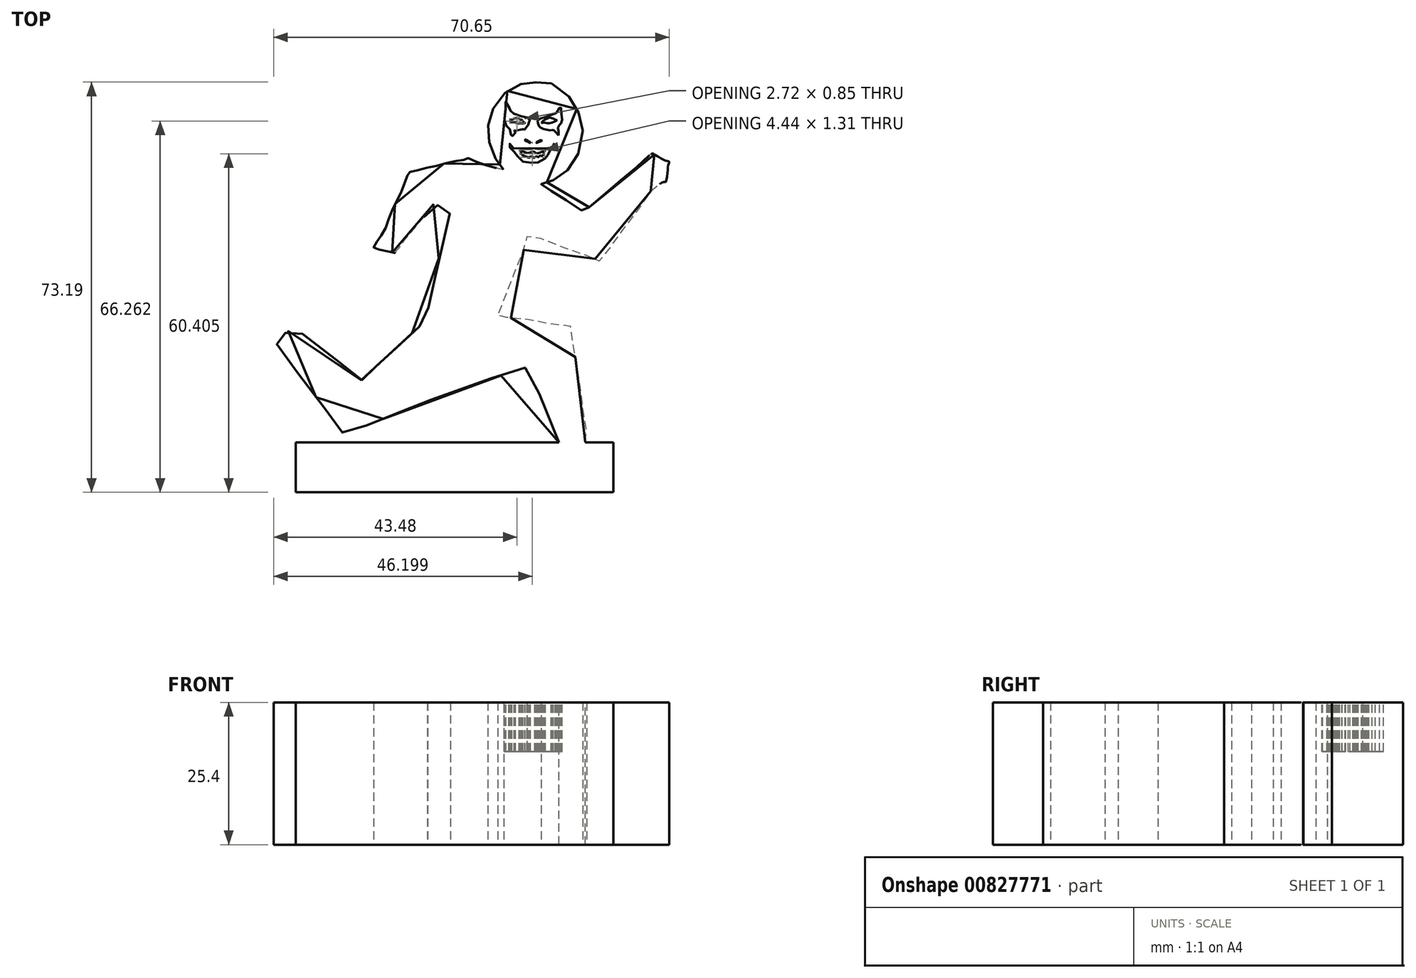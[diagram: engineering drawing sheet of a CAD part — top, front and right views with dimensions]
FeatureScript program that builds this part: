
annotation { "Feature Type Name" : "Feature", "Feature Type Description" : "" }
export const myFeature = defineFeature(function(context is Context, id is Id, definition is map)
    precondition{}
    {
        {
            var Q0;
            Q0=qCreatedBy(makeId("Top.planeOp"),FACE);
            var sketch = newSketch(context, id + "F0", { "sketchPlane" : qUnion([Q0])});
            skFitSpline(sketch, "E0", {"points": [v(-18.57, 4.15) * mm, v(-18.19, 6.36) * mm, v(-17.9, 8.2) * mm, v(-17.86, 8.65) * mm, v(-18.13, 9.75) * mm, v(-18.45, 11.85) * mm, v(-18.86, 15.21) * mm, v(-19.32, 18.61) * mm, v(-20.02, 22.59) * mm, v(-20.53, 26.32) * mm, v(-20.61, 27.35) * mm, v(-21.3, 27.55) * mm, v(-24.68, 27.94) * mm, v(-27.86, 28.57) * mm, v(-31.24, 28.92) * mm, v(-33.01, 29.13) * mm, v(-33.54, 29.19) * mm, v(-33.74, 29.28) * mm, v(-33.32, 30.3) * mm, v(-32.15, 33.5) * mm, v(-30.8, 36.86) * mm, v(-29.46, 40.17) * mm, v(-28.8, 42.23) * mm, v(-28.38, 43.77) * mm, v(-28.1, 44) * mm, v(-25.31, 42.81) * mm, v(-21.7, 41.41) * mm, v(-18.29, 40.28) * mm, v(-16.26, 39.46) * mm, v(-15.7, 39.1) * mm, v(-15.31, 39.32) * mm, v(-13.92, 41.12) * mm, v(-12.37, 43.38) * mm, v(-9, 47.86) * mm, v(-6.92, 50.75) * mm, v(-6.19, 51.93) * mm, v(-5.77, 52.26) * mm, v(-5.17, 52.66) * mm, v(-3.98, 53.25) * mm, v(-3.78, 53.22) * mm, v(-3.46, 54.96) * mm, v(-3.26, 56.4) * mm, v(-3.15, 56.8) * mm, v(-3.63, 56.97) * mm, v(-4.66, 57.47) * mm, v(-5.8, 58.12) * mm, v(-6.13, 58.31) * mm, v(-7.33, 57.4) * mm, v(-8.86, 55.97) * mm, v(-11.18, 54.03) * mm, v(-13.45, 52.12) * mm, v(-15.8, 50.1) * mm, v(-17.86, 48.26) * mm, v(-18.18, 47.89) * mm, v(-18.46, 47.96) * mm, v(-19.96, 48.87) * mm, v(-22.15, 50.4) * mm, v(-23.95, 51.46) * mm, v(-25.32, 52.34) * mm, v(-25.89, 52.72) * mm, v(-26.03, 52.96) * mm, v(-24.8, 53.2) * mm, v(-22.93, 54.05) * mm, v(-21.15, 55.45) * mm, v(-19.69, 57.6) * mm, v(-18.57, 61.62) * mm, v(-18.94, 64.38) * mm, v(-19.76, 66.54) * mm, v(-21.27, 68.72) * mm, v(-24.1, 70.74) * mm, v(-25.79, 70.95) * mm, v(-27.57, 71.03) * mm, v(-29.04, 70.86) * mm, v(-31.2, 69.95) * mm, v(-33.06, 68.54) * mm, v(-34.62, 66.1) * mm, v(-35.35, 63.99) * mm, v(-35.5, 62.12) * mm, v(-35.21, 60) * mm, v(-34.46, 57.88) * mm, v(-33.2, 56.14) * mm, v(-32.7, 55.5) * mm, v(-33.8, 55.63) * mm, v(-36.24, 56.34) * mm, v(-38.3, 57.1) * mm, v(-39.38, 57.5) * mm, v(-39.79, 57.18) * mm, v(-40.83, 57) * mm, v(-43.05, 56.57) * mm, v(-45.2, 55.97) * mm, v(-47.08, 55.56) * mm, v(-48.97, 55.06) * mm, v(-49.7, 54.93) * mm, v(-49.85, 54.55) * mm, v(-50.25, 53.43) * mm, v(-51.04, 51.35) * mm, v(-52.04, 49.37) * mm, v(-52.93, 47.45) * mm, v(-53.51, 45.7) * mm, v(-54.33, 43.98) * mm, v(-55.15, 42.91) * mm, v(-55.63, 41.9) * mm, v(-55.92, 41.43) * mm, v(-54.9, 41.14) * mm, v(-52.72, 40.62) * mm, v(-52.08, 40.47) * mm, v(-51.93, 40.79) * mm, v(-51.3, 41.51) * mm, v(-50.52, 42.7) * mm, v(-48.89, 44.6) * mm, v(-47.55, 46.27) * mm, v(-46.29, 47.66) * mm, v(-45.47, 48.87) * mm, v(-45.26, 49.22) * mm, v(-44.65, 49.12) * mm, v(-43.31, 48.79) * mm, v(-42.65, 48.66) * mm, v(-42.26, 48.5) * mm, v(-42.33, 47.66) * mm, v(-42.76, 46.23) * mm, v(-43.3, 43.25) * mm, v(-43.93, 40.96) * mm, v(-44.64, 37.9) * mm, v(-45.18, 34.92) * mm, v(-45.7, 32.63) * mm, v(-46.33, 29.56) * mm, v(-46.32, 28.72) * mm, v(-46.61, 28.55) * mm, v(-47.86, 27.33) * mm, v(-50.02, 25.33) * mm, v(-51.73, 23.7) * mm, v(-53.4, 22.14) * mm, v(-54.77, 20.94) * mm, v(-55.8, 20) * mm, v(-56.88, 18.93) * mm, v(-57.76, 18.1) * mm, v(-57.87, 17.9) * mm, v(-58.09, 17.85) * mm, v(-59.2, 18.82) * mm, v(-62.6, 21.46) * mm, v(-66.37, 24.44) * mm, v(-69.48, 26.81) * mm, v(-70.18, 27.28) * mm, v(-70.64, 26.95) * mm, v(-71.48, 26.4) * mm, v(-73.02, 25.57) * mm, v(-73.68, 25.26) * mm, v(-73.79, 25.07) * mm, v(-73.23, 24.27) * mm, v(-71.8, 22.23) * mm, v(-69.4, 19.03) * mm, v(-65.94, 14.44) * mm, v(-63.46, 11.27) * mm, v(-61.85, 9.03) * mm, v(-61.54, 8.55) * mm, v(-61.24, 8.13) * mm, v(-60.28, 8.47) * mm, v(-57.12, 9.8) * mm, v(-53.29, 11.31) * mm, v(-50.62, 12.42) * mm, v(-48.3, 13.44) * mm, v(-45.41, 14.45) * mm, v(-35.33, 18.05) * mm, v(-30.91, 19.34) * mm, v(-28.87, 20.1) * mm, v(-28.19, 20.07) * mm, v(-27.62, 18.72) * mm, v(-24.93, 11.88) * mm, v(-22.71, 6.44) * mm, v(-22.05, 4.72) * mm, v(-21.8, 4.28) * mm, v(-20.08, 4.35) * mm, v(-18.57, 4.15) * mm]});
            skSolve(sketch);
        }
        {
            var Q0;
            Q0 = qSketchRegion(id + "F0", true);
            extrude(context, id + "F1", {"entities" : qUnion([Q0]), "oppositeDirection" : true, "depth" : 25.4 * mm, "offsetDistance" : 25.4 * mm});
        }
        {
            var Q0;
            Q0=makeQuery(id+"F1.opExtrude","CAP_FACE",FACE,{"disambiguationData":[OSD([sQuery(id+"F0.wireOp",EDGE,"E0")])],"isStart":true});
            var sketch = newSketch(context, id + "F2", { "sketchPlane" : qUnion([Q0])});
            skFitSpline(sketch, "E1", {"points": [v(-31.67, 64.14) * mm, v(-31.52, 64.08) * mm, v(-31.41, 64.03) * mm, v(-31.33, 63.94) * mm, v(-31.24, 63.92) * mm, v(-31.1, 63.93) * mm, v(-31.04, 63.88) * mm, v(-30.93, 63.84) * mm, v(-30.77, 63.8) * mm, v(-30.64, 63.76) * mm, v(-30.5, 63.71) * mm, v(-30.36, 63.67) * mm, v(-30.2, 63.66) * mm, v(-30.09, 63.65) * mm, v(-30, 63.65) * mm, v(-29.9, 63.68) * mm, v(-29.8, 63.7) * mm, v(-29.67, 63.67) * mm, v(-29.5, 63.64) * mm, v(-29.37, 63.66) * mm, v(-29.2, 63.71) * mm, v(-29, 63.7) * mm, v(-28.89, 63.7) * mm, v(-28.9, 63.76) * mm, v(-28.97, 63.87) * mm, v(-29.08, 63.95) * mm, v(-29.22, 64.01) * mm, v(-29.35, 64.12) * mm, v(-29.5, 64.3) * mm, v(-29.6, 64.4) * mm, v(-29.73, 64.45) * mm, v(-30, 64.5) * mm, v(-30.23, 64.54) * mm, v(-30.4, 64.57) * mm, v(-30.58, 64.58) * mm, v(-30.74, 64.57) * mm, v(-30.97, 64.5) * mm, v(-31.18, 64.4) * mm, v(-31.38, 64.3) * mm, v(-31.53, 64.22) * mm, v(-31.67, 64.14) * mm]});
            skFitSpline(sketch, "E2", {"points": [v(-25.97, 63.88) * mm, v(-25.8, 64) * mm, v(-25.53, 64.2) * mm, v(-25.34, 64.35) * mm, v(-25.08, 64.5) * mm, v(-24.68, 64.65) * mm, v(-24.33, 64.66) * mm, v(-23.87, 64.5) * mm, v(-23.5, 64.35) * mm, v(-23.22, 64.22) * mm, v(-23.2, 64.21) * mm, v(-23.29, 64.15) * mm, v(-23.5, 64.05) * mm, v(-23.93, 63.88) * mm, v(-24.2, 63.78) * mm, v(-24.54, 63.7) * mm, v(-24.84, 63.7) * mm, v(-25.23, 63.77) * mm, v(-25.5, 63.81) * mm, v(-25.68, 63.83) * mm, v(-25.72, 63.83) * mm, v(-25.78, 63.76) * mm, v(-25.83, 63.76) * mm, v(-25.87, 63.76) * mm, v(-25.92, 63.8) * mm, v(-25.97, 63.88) * mm]});
            skFitSpline(sketch, "E3", {"points": [v(-26.82, 60.3) * mm, v(-26.6, 60.45) * mm, v(-26.33, 60.6) * mm, v(-26.15, 60.67) * mm, v(-26, 60.69) * mm, v(-25.91, 60.64) * mm, v(-25.9, 60.55) * mm, v(-25.95, 60.52) * mm, v(-26.08, 60.47) * mm, v(-26.23, 60.42) * mm, v(-26.34, 60.38) * mm, v(-26.4, 60.34) * mm, v(-26.52, 60.3) * mm, v(-26.66, 60.25) * mm, v(-26.79, 60.2) * mm, v(-26.9, 60.17) * mm, v(-26.9, 60.2) * mm, v(-26.82, 60.3) * mm]});
            skFitSpline(sketch, "E4", {"points": [v(-27.9, 60.19) * mm, v(-27.9, 60.23) * mm, v(-27.9, 60.24) * mm, v(-27.91, 60.26) * mm, v(-28.02, 60.36) * mm, v(-28.13, 60.43) * mm, v(-28.27, 60.5) * mm, v(-28.35, 60.55) * mm, v(-28.44, 60.6) * mm, v(-28.54, 60.69) * mm, v(-28.65, 60.75) * mm, v(-28.75, 60.78) * mm, v(-28.85, 60.77) * mm, v(-28.9, 60.73) * mm, v(-28.92, 60.7) * mm, v(-28.9, 60.63) * mm, v(-28.84, 60.55) * mm, v(-28.78, 60.51) * mm, v(-28.71, 60.5) * mm, v(-28.63, 60.5) * mm, v(-28.5, 60.44) * mm, v(-28.4, 60.38) * mm, v(-28.3, 60.34) * mm, v(-27.9, 60.19) * mm]});
            skFitSpline(sketch, "E5", {"points": [v(-25.3, 57.41) * mm, v(-25.26, 57.5) * mm, v(-25.2, 57.6) * mm, v(-25.08, 57.74) * mm, v(-24.94, 57.89) * mm, v(-24.8, 58.03) * mm, v(-24.73, 58.1) * mm, v(-24.66, 58.22) * mm, v(-24.6, 58.38) * mm, v(-24.49, 58.64) * mm, v(-24.43, 58.82) * mm, v(-24.41, 58.86) * mm, v(-24.36, 58.9) * mm, v(-24.3, 58.94) * mm, v(-24.23, 58.96) * mm, v(-24.25, 59.03) * mm, v(-24.22, 59.09) * mm, v(-24.15, 59.06) * mm, v(-24.13, 59.12) * mm, v(-24.04, 59.15) * mm, v(-23.94, 59.18) * mm, v(-23.87, 59.21) * mm, v(-23.83, 59.3) * mm, v(-23.84, 59.35) * mm, v(-23.86, 59.4) * mm, v(-23.85, 59.44) * mm, v(-23.85, 59.48) * mm, v(-23.83, 59.5) * mm, v(-23.78, 59.47) * mm, v(-23.69, 59.43) * mm, v(-23.62, 59.44) * mm, v(-23.53, 59.5) * mm, v(-23.45, 59.56) * mm, v(-23.37, 59.69) * mm, v(-23.33, 59.8) * mm, v(-23.37, 59.91) * mm, v(-23.44, 60) * mm, v(-23.54, 60.06) * mm, v(-23.62, 60.1) * mm, v(-23.69, 60.09) * mm, v(-23.73, 60.05) * mm, v(-23.79, 59.99) * mm, v(-23.84, 59.94) * mm, v(-23.88, 59.87) * mm, v(-23.88, 59.83) * mm, v(-23.82, 59.76) * mm, v(-23.82, 59.72) * mm, v(-23.84, 59.67) * mm, v(-23.87, 59.65) * mm, v(-23.92, 59.66) * mm, v(-23.96, 59.7) * mm, v(-23.98, 59.71) * mm, v(-23.94, 59.63) * mm, v(-23.94, 59.57) * mm, v(-23.98, 59.51) * mm, v(-24.02, 59.47) * mm, v(-24.11, 59.41) * mm, v(-24.17, 59.33) * mm, v(-24.28, 59.28) * mm, v(-24.42, 59.25) * mm, v(-24.63, 59.19) * mm, v(-24.8, 59.19) * mm, v(-25.05, 59.19) * mm, v(-25.26, 59.22) * mm, v(-25.4, 59.19) * mm, v(-25.63, 59.2) * mm, v(-25.86, 59.2) * mm, v(-26.12, 59.2) * mm, v(-26.37, 59.22) * mm, v(-26.6, 59.24) * mm, v(-26.87, 59.22) * mm, v(-27.47, 59.06) * mm, v(-27.52, 59.03) * mm, v(-27.6, 59.12) * mm, v(-27.9, 59.22) * mm, v(-28.27, 59.24) * mm, v(-28.63, 59.28) * mm, v(-29.27, 59.25) * mm, v(-29.75, 59.16) * mm, v(-30.36, 59.13) * mm, v(-30.77, 59.18) * mm, v(-31.04, 59.29) * mm, v(-31.16, 59.36) * mm, v(-31.25, 59.38) * mm, v(-31.27, 59.44) * mm, v(-31.33, 59.53) * mm, v(-31.39, 59.58) * mm, v(-31.37, 59.66) * mm, v(-31.33, 59.77) * mm, v(-31.24, 59.86) * mm, v(-31.27, 60.01) * mm, v(-31.33, 60.08) * mm, v(-31.42, 60.05) * mm, v(-31.56, 60.03) * mm, v(-31.67, 59.92) * mm, v(-31.77, 59.79) * mm, v(-31.78, 59.7) * mm, v(-31.67, 59.61) * mm, v(-31.62, 59.45) * mm, v(-31.61, 59.38) * mm, v(-31.44, 59.33) * mm, v(-31.33, 59.2) * mm, v(-31.27, 59.04) * mm, v(-31.05, 58.8) * mm, v(-30.83, 58.62) * mm, v(-30.65, 58.45) * mm, v(-30.44, 58.18) * mm, v(-30.22, 57.83) * mm, v(-29.9, 57.4) * mm, v(-29.66, 57.16) * mm, v(-29.5, 56.99) * mm, v(-28.93, 56.76) * mm, v(-28.3, 56.66) * mm, v(-27.76, 56.61) * mm, v(-27.62, 56.7) * mm, v(-27.48, 56.55) * mm, v(-27.27, 56.61) * mm, v(-26.66, 56.7) * mm, v(-25.95, 56.88) * mm, v(-25.43, 57.12) * mm, v(-25.3, 57.41) * mm]});
            skFitSpline(sketch, "E6", {"points": [v(-29.8, 58.9) * mm, v(-29.83, 58.84) * mm, v(-29.81, 58.8) * mm, v(-29.77, 58.7) * mm, v(-29.76, 58.6) * mm, v(-29.73, 58.52) * mm, v(-29.7, 58.47) * mm, v(-29.65, 58.52) * mm, v(-29.64, 58.49) * mm, v(-29.64, 58.39) * mm, v(-29.62, 58.3) * mm, v(-29.54, 58.25) * mm, v(-29.52, 58.24) * mm, v(-29.5, 58.18) * mm, v(-29.46, 58.14) * mm, v(-29.42, 58.1) * mm, v(-29.42, 58.06) * mm, v(-29.42, 57.97) * mm, v(-29.37, 57.89) * mm, v(-29.3, 57.8) * mm, v(-29.27, 57.74) * mm, v(-29.19, 57.7) * mm, v(-29.08, 57.82) * mm, v(-29.06, 57.85) * mm, v(-28.98, 57.66) * mm, v(-28.91, 57.66) * mm, v(-28.88, 57.64) * mm, v(-28.79, 57.6) * mm, v(-28.7, 57.6) * mm, v(-28.65, 57.61) * mm, v(-28.6, 57.7) * mm, v(-28.55, 57.82) * mm, v(-28.55, 57.85) * mm, v(-28.47, 57.87) * mm, v(-28.47, 57.82) * mm, v(-28.42, 57.66) * mm, v(-28.34, 57.58) * mm, v(-28.19, 57.55) * mm, v(-28.15, 57.53) * mm, v(-28.1, 57.53) * mm, v(-28.06, 57.62) * mm, v(-28.01, 57.79) * mm, v(-28, 57.82) * mm, v(-27.9, 57.8) * mm, v(-27.92, 57.77) * mm, v(-27.92, 57.7) * mm, v(-27.93, 57.61) * mm, v(-27.82, 57.5) * mm, v(-27.77, 57.47) * mm, v(-27.7, 57.5) * mm, v(-27.68, 57.6) * mm, v(-27.62, 57.76) * mm, v(-27.57, 57.94) * mm, v(-27.56, 57.9) * mm, v(-27.52, 57.67) * mm, v(-27.5, 57.53) * mm, v(-27.47, 57.46) * mm, v(-27.34, 57.49) * mm, v(-27.19, 57.59) * mm, v(-27.15, 57.67) * mm, v(-27.15, 57.7) * mm, v(-27.11, 57.62) * mm, v(-26.97, 57.6) * mm, v(-26.92, 57.78) * mm, v(-26.87, 57.62) * mm, v(-26.73, 57.58) * mm, v(-26.62, 57.64) * mm, v(-26.56, 57.84) * mm, v(-26.54, 57.79) * mm, v(-26.43, 57.6) * mm, v(-26.34, 57.6) * mm, v(-26.25, 57.6) * mm, v(-26.2, 57.62) * mm, v(-26.08, 57.7) * mm, v(-26.08, 57.83) * mm, v(-26.12, 57.97) * mm, v(-26.15, 58.18) * mm, v(-26.15, 58.32) * mm, v(-26.08, 58.2) * mm, v(-25.98, 57.9) * mm, v(-25.86, 57.76) * mm, v(-25.8, 57.76) * mm, v(-25.74, 57.82) * mm, v(-25.72, 57.98) * mm, v(-25.74, 58.2) * mm, v(-25.68, 58.03) * mm, v(-25.63, 58.03) * mm, v(-25.63, 58.12) * mm, v(-25.63, 58.24) * mm, v(-25.6, 58.16) * mm, v(-25.52, 58.2) * mm, v(-25.5, 58.3) * mm, v(-25.58, 58.38) * mm, v(-25.45, 58.38) * mm, v(-25.4, 58.47) * mm, v(-25.35, 58.54) * mm, v(-25.26, 58.68) * mm, v(-25.24, 58.81) * mm, v(-25.26, 58.88) * mm, v(-25.32, 58.89) * mm, v(-25.4, 58.78) * mm, v(-25.44, 58.73) * mm, v(-25.46, 58.8) * mm, v(-25.48, 58.86) * mm, v(-25.57, 58.86) * mm, v(-25.66, 58.74) * mm, v(-25.71, 58.67) * mm, v(-25.73, 58.74) * mm, v(-25.8, 58.82) * mm, v(-25.95, 58.74) * mm, v(-26.12, 58.58) * mm, v(-26.16, 58.47) * mm, v(-26.2, 58.54) * mm, v(-26.34, 58.6) * mm, v(-26.47, 58.64) * mm, v(-26.62, 58.56) * mm, v(-26.73, 58.41) * mm, v(-26.75, 58.32) * mm, v(-26.76, 58.38) * mm, v(-26.79, 58.53) * mm, v(-26.87, 58.63) * mm, v(-27.08, 58.66) * mm, v(-27.3, 58.66) * mm, v(-27.43, 58.6) * mm, v(-27.52, 58.46) * mm, v(-27.57, 58.25) * mm, v(-27.61, 58.28) * mm, v(-27.65, 58.38) * mm, v(-27.76, 58.54) * mm, v(-27.84, 58.6) * mm, v(-28.02, 58.65) * mm, v(-28.28, 58.5) * mm, v(-28.4, 58.31) * mm, v(-28.4, 58.38) * mm, v(-28.44, 58.56) * mm, v(-28.68, 58.71) * mm, v(-28.97, 58.65) * mm, v(-29.05, 58.55) * mm, v(-29.12, 58.68) * mm, v(-29.27, 58.76) * mm, v(-29.44, 58.73) * mm, v(-29.53, 58.77) * mm, v(-29.68, 58.78) * mm, v(-29.8, 58.9) * mm]});
            skFitSpline(sketch, "E7", {"points": [v(-32.34, 67.55) * mm, v(-32.35, 67.43) * mm, v(-32.32, 67.3) * mm, v(-32.32, 67.2) * mm, v(-32.43, 67.04) * mm, v(-32.46, 66.94) * mm, v(-32.38, 66.92) * mm, v(-32.34, 66.87) * mm, v(-32.4, 66.82) * mm, v(-32.34, 66.8) * mm, v(-32.33, 66.73) * mm, v(-32.33, 66.42) * mm, v(-32.31, 65.92) * mm, v(-32.28, 65.81) * mm, v(-32.3, 65.77) * mm, v(-32.37, 65.61) * mm, v(-32.45, 65.43) * mm, v(-32.49, 65.25) * mm, v(-32.5, 65.13) * mm, v(-32.55, 65.03) * mm, v(-32.6, 64.68) * mm, v(-32.57, 64.3) * mm, v(-32.49, 64) * mm, v(-32.35, 63.75) * mm, v(-32.26, 63.5) * mm, v(-32.22, 63.28) * mm, v(-32.14, 63.1) * mm, v(-32, 62.93) * mm, v(-31.84, 62.84) * mm, v(-31.7, 62.78) * mm, v(-31.58, 62.62) * mm, v(-31.5, 62.5) * mm, v(-31.45, 62.27) * mm, v(-31.48, 62.08) * mm, v(-31.44, 61.82) * mm, v(-31.43, 61.57) * mm, v(-31.5, 61.49) * mm, v(-31.52, 61.35) * mm, v(-31.41, 61.27) * mm, v(-31.23, 61.28) * mm, v(-31.1, 61.44) * mm, v(-31.04, 61.62) * mm, v(-30.9, 61.73) * mm, v(-30.73, 61.89) * mm, v(-30.6, 62.04) * mm, v(-30.58, 62.07) * mm, v(-30.7, 62.08) * mm, v(-30.79, 62.14) * mm, v(-30.74, 62.13) * mm, v(-30.7, 62.14) * mm, v(-30.77, 62.22) * mm, v(-30.85, 62.39) * mm, v(-30.75, 62.38) * mm, v(-30.4, 62.35) * mm, v(-30.1, 62.38) * mm, v(-29.96, 62.42) * mm, v(-29.94, 62.44) * mm, v(-29.99, 62.5) * mm, v(-29.96, 62.57) * mm, v(-29.85, 62.52) * mm, v(-29.76, 62.53) * mm, v(-29.66, 62.47) * mm, v(-29.6, 62.5) * mm, v(-29.36, 62.59) * mm, v(-29.27, 62.63) * mm, v(-29.3, 62.53) * mm, v(-29.43, 62.46) * mm, v(-29.29, 62.45) * mm, v(-28.97, 62.57) * mm, v(-28.76, 62.66) * mm, v(-28.48, 63) * mm, v(-28.4, 63.3) * mm, v(-28.35, 63.36) * mm, v(-28.3, 63.43) * mm, v(-28.3, 63.5) * mm, v(-28.23, 63.59) * mm, v(-28.23, 63.7) * mm, v(-28.2, 63.76) * mm, v(-28.22, 63.81) * mm, v(-28.21, 63.96) * mm, v(-28.15, 64.07) * mm, v(-28.13, 64.12) * mm, v(-28.06, 64.12) * mm, v(-28.06, 64.2) * mm, v(-28.1, 64.28) * mm, v(-28.1, 64.35) * mm, v(-28.03, 64.26) * mm, v(-28, 64.22) * mm, v(-28.05, 64.35) * mm, v(-28.1, 64.45) * mm, v(-28.12, 64.5) * mm, v(-28.23, 64.53) * mm, v(-28.37, 64.64) * mm, v(-28.4, 64.68) * mm, v(-28.5, 64.68) * mm, v(-28.52, 64.72) * mm, v(-28.9, 64.84) * mm, v(-28.9, 64.78) * mm, v(-28.88, 64.73) * mm, v(-28.9, 64.73) * mm, v(-28.97, 64.81) * mm, v(-29.3, 64.95) * mm, v(-29.35, 64.86) * mm, v(-29.46, 64.92) * mm, v(-29.53, 64.96) * mm, v(-29.55, 64.87) * mm, v(-29.63, 65) * mm, v(-30.01, 65.1) * mm, v(-30.6, 65.27) * mm, v(-30.92, 65.42) * mm, v(-30.94, 65.53) * mm, v(-31.13, 65.5) * mm, v(-31.16, 65.6) * mm, v(-31.26, 65.64) * mm, v(-31.42, 65.85) * mm, v(-31.51, 65.94) * mm, v(-31.47, 65.98) * mm, v(-31.64, 66.08) * mm, v(-31.7, 66.09) * mm, v(-31.61, 66.18) * mm, v(-31.64, 66.28) * mm, v(-31.67, 66.4) * mm, v(-31.93, 66.78) * mm, v(-32.04, 67.04) * mm, v(-32.34, 67.55) * mm]});
            skFitSpline(sketch, "E8", {"points": [v(-22.88, 61.56) * mm, v(-22.84, 61.75) * mm, v(-22.9, 62) * mm, v(-22.86, 62.13) * mm, v(-22.9, 62.35) * mm, v(-22.88, 62.5) * mm, v(-22.97, 62.71) * mm, v(-22.99, 62.86) * mm, v(-23.1, 63) * mm, v(-23.1, 63.08) * mm, v(-22.82, 63.3) * mm, v(-22.78, 63.35) * mm, v(-22.61, 63.39) * mm, v(-22.65, 63.47) * mm, v(-22.52, 63.63) * mm, v(-22.46, 63.62) * mm, v(-22.46, 63.7) * mm, v(-22.39, 63.83) * mm, v(-22.35, 63.93) * mm, v(-22.28, 64.05) * mm, v(-22.27, 64.51) * mm, v(-22.4, 64.94) * mm, v(-22.41, 65.07) * mm, v(-22.42, 65.5) * mm, v(-22.47, 65.93) * mm, v(-22.49, 66.66) * mm, v(-22.58, 66.83) * mm, v(-22.74, 66.67) * mm, v(-22.82, 66.14) * mm, v(-23.03, 65.7) * mm, v(-23.32, 65.53) * mm, v(-23.83, 65.4) * mm, v(-24.23, 65.15) * mm, v(-24.7, 65.05) * mm, v(-25.18, 64.87) * mm, v(-25.6, 64.66) * mm, v(-25.7, 64.65) * mm, v(-26.03, 64.59) * mm, v(-26.31, 64.47) * mm, v(-26.6, 64.34) * mm, v(-26.6, 64.27) * mm, v(-26.64, 64.21) * mm, v(-26.63, 64.01) * mm, v(-26.67, 63.88) * mm, v(-26.6, 63.92) * mm, v(-26.58, 63.8) * mm, v(-26.6, 63.69) * mm, v(-26.61, 63.51) * mm, v(-26.56, 63.41) * mm, v(-26.38, 63.3) * mm, v(-26.4, 63.2) * mm, v(-26.24, 63.07) * mm, v(-26.16, 63.06) * mm, v(-26.08, 63.02) * mm, v(-26.1, 62.95) * mm, v(-26.16, 62.96) * mm, v(-25.98, 62.8) * mm, v(-25.9, 62.82) * mm, v(-25.82, 62.75) * mm, v(-25.68, 62.7) * mm, v(-25.57, 62.7) * mm, v(-25.37, 62.69) * mm, v(-25.28, 62.62) * mm, v(-25.11, 62.56) * mm, v(-24.95, 62.54) * mm, v(-24.88, 62.5) * mm, v(-24.7, 62.45) * mm, v(-24.5, 62.45) * mm, v(-24.33, 62.44) * mm, v(-24.28, 62.49) * mm, v(-24.22, 62.43) * mm, v(-24.06, 62.5) * mm, v(-23.93, 62.5) * mm, v(-23.88, 62.5) * mm, v(-23.86, 62.47) * mm, v(-23.9, 62.42) * mm, v(-23.91, 62.4) * mm, v(-23.85, 62.4) * mm, v(-23.78, 62.42) * mm, v(-23.7, 62.4) * mm, v(-23.6, 62.42) * mm, v(-23.5, 62.29) * mm, v(-23.5, 62.22) * mm, v(-23.43, 62.18) * mm, v(-23.4, 62.06) * mm, v(-23.2, 61.95) * mm, v(-23.12, 61.74) * mm, v(-22.88, 61.56) * mm]});
            skSolve(sketch);
        }
        {
            var Q0;
            Q0 = qSketchRegion(id + "F2", true);
            extrude(context, id + "F3", {"entities" : qUnion([Q0]), "oppositeDirection" : true, "depth" : 8.79 * mm, "offsetDistance" : 25.4 * mm});
        }
        {
            var Q0;
            Q0=qCreatedBy(makeId("Top.planeOp"),FACE);
            var sketch = newSketch(context, id + "F4", { "sketchPlane" : qUnion([Q0])});
            skLineSegment(sketch, "E9.bottom", {"start": v(-69.8, 6.76) * mm, "end": v(-13.1, 6.76) * mm});
            skLineSegment(sketch, "E9.top", {"start": v(-69.8, -2.16) * mm, "end": v(-13.1, -2.16) * mm});
            skLineSegment(sketch, "E9.left", {"start": v(-69.8, 6.76) * mm, "end": v(-69.8, -2.16) * mm});
            skLineSegment(sketch, "E9.right", {"start": v(-13.1, 6.76) * mm, "end": v(-13.1, -2.16) * mm});
            skSolve(sketch);
        }
        {
            var Q0;
            Q0=makeQuery(id+"F4.imprint","IMPRINT",FACE,{"disambiguationData":[TD([[makeQuery(id+"F4.imprint","IMPRINT",EDGE,{"derivedFrom":sQuery(id+"F4.wireOp",EDGE,"E9.bottom")}),-1.0]])]});
            extrude(context, id + "F5", {"entities" : qUnion([Q0]), "operationType" : NewBodyOperationType.ADD, "oppositeDirection" : true, "depth" : 25.4 * mm, "offsetDistance" : 25.4 * mm});
        }
    });
